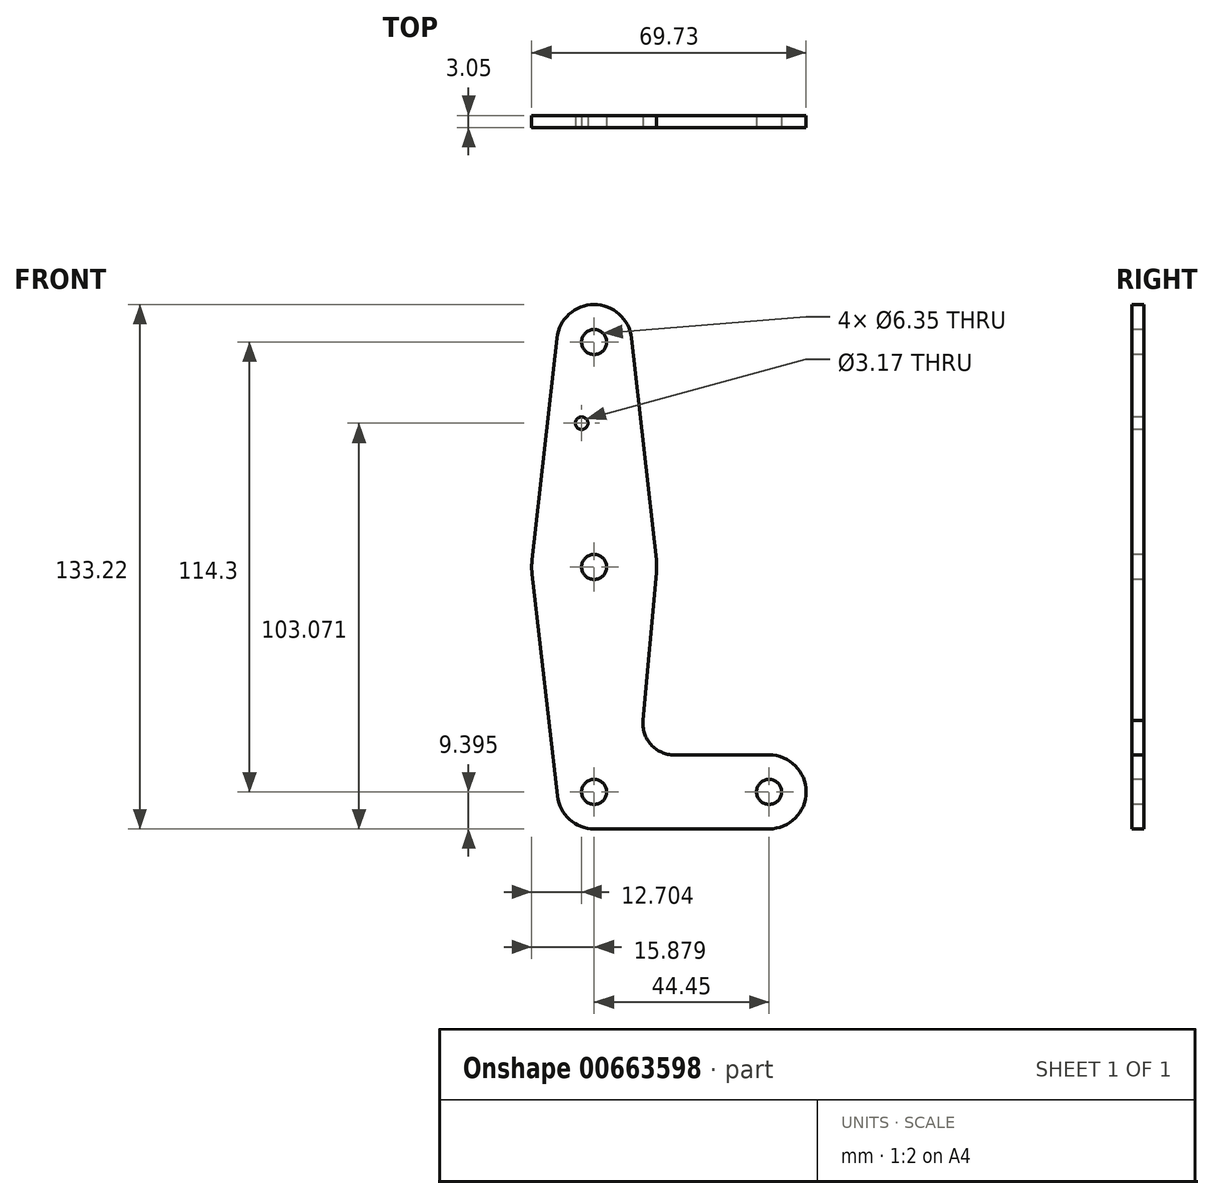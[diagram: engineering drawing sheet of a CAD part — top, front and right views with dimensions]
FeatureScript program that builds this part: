
annotation { "Feature Type Name" : "Feature", "Feature Type Description" : "" }
export const myFeature = defineFeature(function(context is Context, id is Id, definition is map)
    precondition{}
    {
        {
            var Q0;
            Q0=qCreatedBy(makeId("Front.planeOp"),FACE);
            var sketch = newSketch(context, id + "F0", { "sketchPlane" : qUnion([Q0])});
            skLineSegment(sketch, "E0", {"start": v(-45.88, 55.92) * mm, "end": v(-45.88, -58.38) * mm, "construction": true});
            skLineSegment(sketch, "E1", {"start": v(-45.88, -58.38) * mm, "end": v(-1.43, -58.38) * mm, "construction": true});
            skCircle(sketch, "E2", {"center": v(-45.88, 55.92) * mm, "radius": 9.53 * mm});
            skCircle(sketch, "E3", {"center": v(-45.88, -1.23) * mm, "radius": 15.88 * mm});
            skCircle(sketch, "E4", {"center": v(-45.88, -58.38) * mm, "radius": 9.4 * mm});
            skCircle(sketch, "E5", {"center": v(-1.43, -58.38) * mm, "radius": 9.4 * mm});
            skLineSegment(sketch, "E6", {"start": v(-55.35, 56.97) * mm, "end": v(-61.66, 0.53) * mm});
            skLineSegment(sketch, "E7", {"start": v(-61.66, -3) * mm, "end": v(-55.22, -59.45) * mm});
            skLineSegment(sketch, "E8", {"start": v(-45.88, -67.78) * mm, "end": v(-1.43, -67.78) * mm});
            skLineSegment(sketch, "E9", {"start": v(-36.41, 56.97) * mm, "end": v(-30.1, 0.53) * mm});
            skLineSegment(sketch, "E10", {"start": v(-1.43, -48.99) * mm, "end": v(-25.55, -48.99) * mm});
            skPoint(sketch, "E11.orphan", {"position": v(-30.1, -3) * mm});
            skCircle(sketch, "E12", {"center": v(-45.88, -1.23) * mm, "radius": 3.18 * mm});
            skCircle(sketch, "E13", {"center": v(-45.88, -58.38) * mm, "radius": 3.18 * mm});
            skCircle(sketch, "E14", {"center": v(-45.88, 55.92) * mm, "radius": 3.18 * mm});
            skCircle(sketch, "E15", {"center": v(-1.43, -58.38) * mm, "radius": 3.18 * mm});
            skCircle(sketch, "E16", {"center": v(-49.06, 35.3) * mm, "radius": 1.59 * mm});
            skArc(sketch, "E17.filletArc", {"start": v(-33.46, -40.21) * mm, "mid": v(-31.46, -46.36) * mm, "end": v(-25.55, -48.99) * mm});
            skLineSegment(sketch, "E18", {"start": v(-33.46, -40.21) * mm, "end": v(-30.07, -2.66) * mm});
            skText(sketch, "E19", { "text": "ben cahill\n\n0.728in3", "fontName": "OpenSans-Regular.ttf"});
            const initialGuessF0  = {"E19": [0.02328, 0.10574, 1, 0, 0.01949]};
            skSetInitialGuess(sketch, initialGuessF0);
            skSolve(sketch);
        }
        {
            var Q0;
            Q0 = qSketchRegion(id + "F0", true);
            extrude(context, id + "F1", {"entities" : qUnion([Q0]), "oppositeDirection" : true, "depth" : 3.05 * mm, "offsetDistance" : 25.4 * mm});
        }
        {
            var Q0;
            Q0=makeQuery(id+"F1.opExtrude","SWEPT_BODY",BODY,{"disambiguationData":[OSD([sQuery(id+"F0.wireOp",EDGE,"E19.sketch_text.stroke-0"),sQuery(id+"F0.wireOp",EDGE,"E19.sketch_text.stroke-1"),sQuery(id+"F0.wireOp",EDGE,"E19.sketch_text.stroke-2"),sQuery(id+"F0.wireOp",EDGE,"E19.sketch_text.stroke-3"),sQuery(id+"F0.wireOp",EDGE,"E19.sketch_text.stroke-4"),sQuery(id+"F0.wireOp",EDGE,"E19.sketch_text.stroke-5"),sQuery(id+"F0.wireOp",EDGE,"E19.sketch_text.stroke-6"),sQuery(id+"F0.wireOp",EDGE,"E19.sketch_text.stroke-7"),sQuery(id+"F0.wireOp",EDGE,"E19.sketch_text.stroke-8"),sQuery(id+"F0.wireOp",EDGE,"E19.sketch_text.stroke-9"),sQuery(id+"F0.wireOp",EDGE,"E19.sketch_text.stroke-10"),sQuery(id+"F0.wireOp",EDGE,"E19.sketch_text.stroke-11"),sQuery(id+"F0.wireOp",EDGE,"E19.sketch_text.stroke-12"),sQuery(id+"F0.wireOp",EDGE,"E19.sketch_text.stroke-13"),sQuery(id+"F0.wireOp",EDGE,"E19.sketch_text.stroke-14"),sQuery(id+"F0.wireOp",EDGE,"E19.sketch_text.stroke-15"),sQuery(id+"F0.wireOp",EDGE,"E19.sketch_text.stroke-16"),sQuery(id+"F0.wireOp",EDGE,"E19.sketch_text.stroke-17"),sQuery(id+"F0.wireOp",EDGE,"E19.sketch_text.stroke-18"),sQuery(id+"F0.wireOp",EDGE,"E19.sketch_text.stroke-19"),sQuery(id+"F0.wireOp",EDGE,"E19.sketch_text.stroke-20"),sQuery(id+"F0.wireOp",EDGE,"E19.sketch_text.stroke-21"),sQuery(id+"F0.wireOp",EDGE,"E19.sketch_text.stroke-22")])]});
            var Q1;
            Q1=makeQuery(id+"F1.opExtrude","SWEPT_BODY",BODY,{"disambiguationData":[OSD([sQuery(id+"F0.wireOp",EDGE,"E19.sketch_text.stroke-23"),sQuery(id+"F0.wireOp",EDGE,"E19.sketch_text.stroke-24"),sQuery(id+"F0.wireOp",EDGE,"E19.sketch_text.stroke-25"),sQuery(id+"F0.wireOp",EDGE,"E19.sketch_text.stroke-26"),sQuery(id+"F0.wireOp",EDGE,"E19.sketch_text.stroke-27"),sQuery(id+"F0.wireOp",EDGE,"E19.sketch_text.stroke-28"),sQuery(id+"F0.wireOp",EDGE,"E19.sketch_text.stroke-29"),sQuery(id+"F0.wireOp",EDGE,"E19.sketch_text.stroke-30"),sQuery(id+"F0.wireOp",EDGE,"E19.sketch_text.stroke-31"),sQuery(id+"F0.wireOp",EDGE,"E19.sketch_text.stroke-32"),sQuery(id+"F0.wireOp",EDGE,"E19.sketch_text.stroke-33"),sQuery(id+"F0.wireOp",EDGE,"E19.sketch_text.stroke-34"),sQuery(id+"F0.wireOp",EDGE,"E19.sketch_text.stroke-35"),sQuery(id+"F0.wireOp",EDGE,"E19.sketch_text.stroke-36"),sQuery(id+"F0.wireOp",EDGE,"E19.sketch_text.stroke-37"),sQuery(id+"F0.wireOp",EDGE,"E19.sketch_text.stroke-38"),sQuery(id+"F0.wireOp",EDGE,"E19.sketch_text.stroke-39"),sQuery(id+"F0.wireOp",EDGE,"E19.sketch_text.stroke-40"),sQuery(id+"F0.wireOp",EDGE,"E19.sketch_text.stroke-41")])]});
            deleteBodies(context, id + "F2", {"entities" : qUnion([Q0, Q1])});
        }
        {
            var Q0;
            Q0=makeQuery(id+"F1.opExtrude","SWEPT_BODY",BODY,{"disambiguationData":[OSD([sQuery(id+"F0.wireOp",EDGE,"E19.sketch_text.stroke-42"),sQuery(id+"F0.wireOp",EDGE,"E19.sketch_text.stroke-43"),sQuery(id+"F0.wireOp",EDGE,"E19.sketch_text.stroke-44"),sQuery(id+"F0.wireOp",EDGE,"E19.sketch_text.stroke-45"),sQuery(id+"F0.wireOp",EDGE,"E19.sketch_text.stroke-46"),sQuery(id+"F0.wireOp",EDGE,"E19.sketch_text.stroke-47"),sQuery(id+"F0.wireOp",EDGE,"E19.sketch_text.stroke-48"),sQuery(id+"F0.wireOp",EDGE,"E19.sketch_text.stroke-49"),sQuery(id+"F0.wireOp",EDGE,"E19.sketch_text.stroke-50"),sQuery(id+"F0.wireOp",EDGE,"E19.sketch_text.stroke-51"),sQuery(id+"F0.wireOp",EDGE,"E19.sketch_text.stroke-52"),sQuery(id+"F0.wireOp",EDGE,"E19.sketch_text.stroke-53"),sQuery(id+"F0.wireOp",EDGE,"E19.sketch_text.stroke-54"),sQuery(id+"F0.wireOp",EDGE,"E19.sketch_text.stroke-55"),sQuery(id+"F0.wireOp",EDGE,"E19.sketch_text.stroke-56"),sQuery(id+"F0.wireOp",EDGE,"E19.sketch_text.stroke-57"),sQuery(id+"F0.wireOp",EDGE,"E19.sketch_text.stroke-58")])]});
            deleteBodies(context, id + "F3", {"entities" : qUnion([Q0])});
        }
        {
            var Q0;
            Q0=makeQuery(id+"F1.opExtrude","SWEPT_BODY",BODY,{"disambiguationData":[OSD([sQuery(id+"F0.wireOp",EDGE,"E19.sketch_text.stroke-101"),sQuery(id+"F0.wireOp",EDGE,"E19.sketch_text.stroke-102"),sQuery(id+"F0.wireOp",EDGE,"E19.sketch_text.stroke-103"),sQuery(id+"F0.wireOp",EDGE,"E19.sketch_text.stroke-104"),sQuery(id+"F0.wireOp",EDGE,"E19.sketch_text.stroke-105"),sQuery(id+"F0.wireOp",EDGE,"E19.sketch_text.stroke-106"),sQuery(id+"F0.wireOp",EDGE,"E19.sketch_text.stroke-107"),sQuery(id+"F0.wireOp",EDGE,"E19.sketch_text.stroke-108"),sQuery(id+"F0.wireOp",EDGE,"E19.sketch_text.stroke-109"),sQuery(id+"F0.wireOp",EDGE,"E19.sketch_text.stroke-110"),sQuery(id+"F0.wireOp",EDGE,"E19.sketch_text.stroke-111"),sQuery(id+"F0.wireOp",EDGE,"E19.sketch_text.stroke-112"),sQuery(id+"F0.wireOp",EDGE,"E19.sketch_text.stroke-113"),sQuery(id+"F0.wireOp",EDGE,"E19.sketch_text.stroke-114"),sQuery(id+"F0.wireOp",EDGE,"E19.sketch_text.stroke-115"),sQuery(id+"F0.wireOp",EDGE,"E19.sketch_text.stroke-116"),sQuery(id+"F0.wireOp",EDGE,"E19.sketch_text.stroke-117"),sQuery(id+"F0.wireOp",EDGE,"E19.sketch_text.stroke-118")])]});
            deleteBodies(context, id + "F4", {"entities" : qUnion([Q0])});
        }
        {
            var Q0;
            Q0=makeQuery(id+"F1.opExtrude","SWEPT_BODY",BODY,{"disambiguationData":[OSD([sQuery(id+"F0.wireOp",EDGE,"E19.sketch_text.stroke-74"),sQuery(id+"F0.wireOp",EDGE,"E19.sketch_text.stroke-75"),sQuery(id+"F0.wireOp",EDGE,"E19.sketch_text.stroke-76"),sQuery(id+"F0.wireOp",EDGE,"E19.sketch_text.stroke-77"),sQuery(id+"F0.wireOp",EDGE,"E19.sketch_text.stroke-78"),sQuery(id+"F0.wireOp",EDGE,"E19.sketch_text.stroke-79"),sQuery(id+"F0.wireOp",EDGE,"E19.sketch_text.stroke-80"),sQuery(id+"F0.wireOp",EDGE,"E19.sketch_text.stroke-81"),sQuery(id+"F0.wireOp",EDGE,"E19.sketch_text.stroke-82"),sQuery(id+"F0.wireOp",EDGE,"E19.sketch_text.stroke-83"),sQuery(id+"F0.wireOp",EDGE,"E19.sketch_text.stroke-84"),sQuery(id+"F0.wireOp",EDGE,"E19.sketch_text.stroke-85"),sQuery(id+"F0.wireOp",EDGE,"E19.sketch_text.stroke-86"),sQuery(id+"F0.wireOp",EDGE,"E19.sketch_text.stroke-87"),sQuery(id+"F0.wireOp",EDGE,"E19.sketch_text.stroke-88"),sQuery(id+"F0.wireOp",EDGE,"E19.sketch_text.stroke-89"),sQuery(id+"F0.wireOp",EDGE,"E19.sketch_text.stroke-90"),sQuery(id+"F0.wireOp",EDGE,"E19.sketch_text.stroke-91"),sQuery(id+"F0.wireOp",EDGE,"E19.sketch_text.stroke-92"),sQuery(id+"F0.wireOp",EDGE,"E19.sketch_text.stroke-93"),sQuery(id+"F0.wireOp",EDGE,"E19.sketch_text.stroke-94"),sQuery(id+"F0.wireOp",EDGE,"E19.sketch_text.stroke-95"),sQuery(id+"F0.wireOp",EDGE,"E19.sketch_text.stroke-96"),sQuery(id+"F0.wireOp",EDGE,"E19.sketch_text.stroke-97"),sQuery(id+"F0.wireOp",EDGE,"E19.sketch_text.stroke-98"),sQuery(id+"F0.wireOp",EDGE,"E19.sketch_text.stroke-99"),sQuery(id+"F0.wireOp",EDGE,"E19.sketch_text.stroke-100")])]});
            deleteBodies(context, id + "F5", {"entities" : qUnion([Q0])});
        }
        {
            var Q0;
            Q0=makeQuery(id+"F1.opExtrude","SWEPT_BODY",BODY,{"disambiguationData":[OSD([sQuery(id+"F0.wireOp",EDGE,"E19.sketch_text.stroke-59"),sQuery(id+"F0.wireOp",EDGE,"E19.sketch_text.stroke-60"),sQuery(id+"F0.wireOp",EDGE,"E19.sketch_text.stroke-61"),sQuery(id+"F0.wireOp",EDGE,"E19.sketch_text.stroke-62"),sQuery(id+"F0.wireOp",EDGE,"E19.sketch_text.stroke-63"),sQuery(id+"F0.wireOp",EDGE,"E19.sketch_text.stroke-64"),sQuery(id+"F0.wireOp",EDGE,"E19.sketch_text.stroke-65"),sQuery(id+"F0.wireOp",EDGE,"E19.sketch_text.stroke-66"),sQuery(id+"F0.wireOp",EDGE,"E19.sketch_text.stroke-67"),sQuery(id+"F0.wireOp",EDGE,"E19.sketch_text.stroke-68"),sQuery(id+"F0.wireOp",EDGE,"E19.sketch_text.stroke-69"),sQuery(id+"F0.wireOp",EDGE,"E19.sketch_text.stroke-70"),sQuery(id+"F0.wireOp",EDGE,"E19.sketch_text.stroke-71"),sQuery(id+"F0.wireOp",EDGE,"E19.sketch_text.stroke-72"),sQuery(id+"F0.wireOp",EDGE,"E19.sketch_text.stroke-73")])]});
            var Q1;
            Q1=makeQuery(id+"F1.opExtrude","SWEPT_BODY",BODY,{"disambiguationData":[OSD([sQuery(id+"F0.wireOp",EDGE,"E19.sketch_text.stroke-119"),sQuery(id+"F0.wireOp",EDGE,"E19.sketch_text.stroke-120"),sQuery(id+"F0.wireOp",EDGE,"E19.sketch_text.stroke-121"),sQuery(id+"F0.wireOp",EDGE,"E19.sketch_text.stroke-122")])]});
            var Q2;
            Q2=makeQuery(id+"F1.opExtrude","SWEPT_BODY",BODY,{"disambiguationData":[OSD([sQuery(id+"F0.wireOp",EDGE,"E19.sketch_text.stroke-123"),sQuery(id+"F0.wireOp",EDGE,"E19.sketch_text.stroke-124"),sQuery(id+"F0.wireOp",EDGE,"E19.sketch_text.stroke-125"),sQuery(id+"F0.wireOp",EDGE,"E19.sketch_text.stroke-126"),sQuery(id+"F0.wireOp",EDGE,"E19.sketch_text.stroke-127"),sQuery(id+"F0.wireOp",EDGE,"E19.sketch_text.stroke-128"),sQuery(id+"F0.wireOp",EDGE,"E19.sketch_text.stroke-129"),sQuery(id+"F0.wireOp",EDGE,"E19.sketch_text.stroke-130")])]});
            deleteBodies(context, id + "F6", {"entities" : qUnion([Q0, Q1, Q2])});
        }
        {
            var Q0;
            Q0=makeQuery(id+"F1.opExtrude","SWEPT_BODY",BODY,{"disambiguationData":[OSD([sQuery(id+"F0.wireOp",EDGE,"E19.sketch_text.stroke-131"),sQuery(id+"F0.wireOp",EDGE,"E19.sketch_text.stroke-132"),sQuery(id+"F0.wireOp",EDGE,"E19.sketch_text.stroke-133"),sQuery(id+"F0.wireOp",EDGE,"E19.sketch_text.stroke-134")])]});
            var Q1;
            Q1=makeQuery(id+"F1.opExtrude","SWEPT_BODY",BODY,{"disambiguationData":[OSD([sQuery(id+"F0.wireOp",EDGE,"E19.sketch_text.stroke-135"),sQuery(id+"F0.wireOp",EDGE,"E19.sketch_text.stroke-136"),sQuery(id+"F0.wireOp",EDGE,"E19.sketch_text.stroke-137"),sQuery(id+"F0.wireOp",EDGE,"E19.sketch_text.stroke-138")])]});
            var Q2;
            Q2=makeQuery(id+"F1.opExtrude","SWEPT_BODY",BODY,{"disambiguationData":[OSD([sQuery(id+"F0.wireOp",EDGE,"E19.sketch_text.stroke-139"),sQuery(id+"F0.wireOp",EDGE,"E19.sketch_text.stroke-140"),sQuery(id+"F0.wireOp",EDGE,"E19.sketch_text.stroke-141"),sQuery(id+"F0.wireOp",EDGE,"E19.sketch_text.stroke-142"),sQuery(id+"F0.wireOp",EDGE,"E19.sketch_text.stroke-143"),sQuery(id+"F0.wireOp",EDGE,"E19.sketch_text.stroke-144"),sQuery(id+"F0.wireOp",EDGE,"E19.sketch_text.stroke-145"),sQuery(id+"F0.wireOp",EDGE,"E19.sketch_text.stroke-146"),sQuery(id+"F0.wireOp",EDGE,"E19.sketch_text.stroke-147"),sQuery(id+"F0.wireOp",EDGE,"E19.sketch_text.stroke-148"),sQuery(id+"F0.wireOp",EDGE,"E19.sketch_text.stroke-149"),sQuery(id+"F0.wireOp",EDGE,"E19.sketch_text.stroke-150"),sQuery(id+"F0.wireOp",EDGE,"E19.sketch_text.stroke-151"),sQuery(id+"F0.wireOp",EDGE,"E19.sketch_text.stroke-152"),sQuery(id+"F0.wireOp",EDGE,"E19.sketch_text.stroke-153"),sQuery(id+"F0.wireOp",EDGE,"E19.sketch_text.stroke-154")])]});
            deleteBodies(context, id + "F7", {"entities" : qUnion([Q0, Q1, Q2])});
        }
        {
            var Q0;
            Q0=makeQuery(id+"F1.opExtrude","SWEPT_BODY",BODY,{"disambiguationData":[OSD([sQuery(id+"F0.wireOp",EDGE,"E19.sketch_text.stroke-155"),sQuery(id+"F0.wireOp",EDGE,"E19.sketch_text.stroke-156"),sQuery(id+"F0.wireOp",EDGE,"E19.sketch_text.stroke-157"),sQuery(id+"F0.wireOp",EDGE,"E19.sketch_text.stroke-158"),sQuery(id+"F0.wireOp",EDGE,"E19.sketch_text.stroke-159"),sQuery(id+"F0.wireOp",EDGE,"E19.sketch_text.stroke-160"),sQuery(id+"F0.wireOp",EDGE,"E19.sketch_text.stroke-161"),sQuery(id+"F0.wireOp",EDGE,"E19.sketch_text.stroke-162")])]});
            deleteBodies(context, id + "F8", {"entities" : qUnion([Q0])});
        }
        {
            var Q0;
            Q0=makeQuery(id+"F1.opExtrude","SWEPT_BODY",BODY,{"disambiguationData":[OSD([sQuery(id+"F0.wireOp",EDGE,"E19.sketch_text.stroke-163"),sQuery(id+"F0.wireOp",EDGE,"E19.sketch_text.stroke-164"),sQuery(id+"F0.wireOp",EDGE,"E19.sketch_text.stroke-165"),sQuery(id+"F0.wireOp",EDGE,"E19.sketch_text.stroke-166"),sQuery(id+"F0.wireOp",EDGE,"E19.sketch_text.stroke-167"),sQuery(id+"F0.wireOp",EDGE,"E19.sketch_text.stroke-168"),sQuery(id+"F0.wireOp",EDGE,"E19.sketch_text.stroke-169")])]});
            deleteBodies(context, id + "F9", {"entities" : qUnion([Q0])});
        }
        {
            var Q0;
            Q0=makeQuery(id+"F1.opExtrude","SWEPT_BODY",BODY,{"disambiguationData":[OSD([sQuery(id+"F0.wireOp",EDGE,"E19.sketch_text.stroke-170"),sQuery(id+"F0.wireOp",EDGE,"E19.sketch_text.stroke-171"),sQuery(id+"F0.wireOp",EDGE,"E19.sketch_text.stroke-172"),sQuery(id+"F0.wireOp",EDGE,"E19.sketch_text.stroke-173"),sQuery(id+"F0.wireOp",EDGE,"E19.sketch_text.stroke-174"),sQuery(id+"F0.wireOp",EDGE,"E19.sketch_text.stroke-175"),sQuery(id+"F0.wireOp",EDGE,"E19.sketch_text.stroke-176"),sQuery(id+"F0.wireOp",EDGE,"E19.sketch_text.stroke-177"),sQuery(id+"F0.wireOp",EDGE,"E19.sketch_text.stroke-178"),sQuery(id+"F0.wireOp",EDGE,"E19.sketch_text.stroke-179"),sQuery(id+"F0.wireOp",EDGE,"E19.sketch_text.stroke-180"),sQuery(id+"F0.wireOp",EDGE,"E19.sketch_text.stroke-181"),sQuery(id+"F0.wireOp",EDGE,"E19.sketch_text.stroke-182"),sQuery(id+"F0.wireOp",EDGE,"E19.sketch_text.stroke-183"),sQuery(id+"F0.wireOp",EDGE,"E19.sketch_text.stroke-184"),sQuery(id+"F0.wireOp",EDGE,"E19.sketch_text.stroke-185"),sQuery(id+"F0.wireOp",EDGE,"E19.sketch_text.stroke-186"),sQuery(id+"F0.wireOp",EDGE,"E19.sketch_text.stroke-187"),sQuery(id+"F0.wireOp",EDGE,"E19.sketch_text.stroke-188"),sQuery(id+"F0.wireOp",EDGE,"E19.sketch_text.stroke-189")])]});
            deleteBodies(context, id + "F10", {"entities" : qUnion([Q0])});
        }
        {
            var Q0;
            Q0=makeQuery(id+"F1.opExtrude","SWEPT_BODY",BODY,{"disambiguationData":[OSD([sQuery(id+"F0.wireOp",EDGE,"E19.sketch_text.stroke-190"),sQuery(id+"F0.wireOp",EDGE,"E19.sketch_text.stroke-191"),sQuery(id+"F0.wireOp",EDGE,"E19.sketch_text.stroke-192"),sQuery(id+"F0.wireOp",EDGE,"E19.sketch_text.stroke-193"),sQuery(id+"F0.wireOp",EDGE,"E19.sketch_text.stroke-194"),sQuery(id+"F0.wireOp",EDGE,"E19.sketch_text.stroke-195"),sQuery(id+"F0.wireOp",EDGE,"E19.sketch_text.stroke-196"),sQuery(id+"F0.wireOp",EDGE,"E19.sketch_text.stroke-197"),sQuery(id+"F0.wireOp",EDGE,"E19.sketch_text.stroke-198"),sQuery(id+"F0.wireOp",EDGE,"E19.sketch_text.stroke-199"),sQuery(id+"F0.wireOp",EDGE,"E19.sketch_text.stroke-200"),sQuery(id+"F0.wireOp",EDGE,"E19.sketch_text.stroke-201"),sQuery(id+"F0.wireOp",EDGE,"E19.sketch_text.stroke-202"),sQuery(id+"F0.wireOp",EDGE,"E19.sketch_text.stroke-203"),sQuery(id+"F0.wireOp",EDGE,"E19.sketch_text.stroke-204"),sQuery(id+"F0.wireOp",EDGE,"E19.sketch_text.stroke-205"),sQuery(id+"F0.wireOp",EDGE,"E19.sketch_text.stroke-206"),sQuery(id+"F0.wireOp",EDGE,"E19.sketch_text.stroke-207"),sQuery(id+"F0.wireOp",EDGE,"E19.sketch_text.stroke-208"),sQuery(id+"F0.wireOp",EDGE,"E19.sketch_text.stroke-209"),sQuery(id+"F0.wireOp",EDGE,"E19.sketch_text.stroke-210"),sQuery(id+"F0.wireOp",EDGE,"E19.sketch_text.stroke-211"),sQuery(id+"F0.wireOp",EDGE,"E19.sketch_text.stroke-212"),sQuery(id+"F0.wireOp",EDGE,"E19.sketch_text.stroke-213"),sQuery(id+"F0.wireOp",EDGE,"E19.sketch_text.stroke-214"),sQuery(id+"F0.wireOp",EDGE,"E19.sketch_text.stroke-215"),sQuery(id+"F0.wireOp",EDGE,"E19.sketch_text.stroke-216"),sQuery(id+"F0.wireOp",EDGE,"E19.sketch_text.stroke-217"),sQuery(id+"F0.wireOp",EDGE,"E19.sketch_text.stroke-218"),sQuery(id+"F0.wireOp",EDGE,"E19.sketch_text.stroke-219"),sQuery(id+"F0.wireOp",EDGE,"E19.sketch_text.stroke-220")])]});
            deleteBodies(context, id + "F11", {"entities" : qUnion([Q0])});
        }
        {
            var Q0;
            Q0=makeQuery(id+"F1.opExtrude","SWEPT_BODY",BODY,{"disambiguationData":[OSD([sQuery(id+"F0.wireOp",EDGE,"E19.sketch_text.stroke-221"),sQuery(id+"F0.wireOp",EDGE,"E19.sketch_text.stroke-222"),sQuery(id+"F0.wireOp",EDGE,"E19.sketch_text.stroke-223"),sQuery(id+"F0.wireOp",EDGE,"E19.sketch_text.stroke-224")])]});
            deleteBodies(context, id + "F12", {"entities" : qUnion([Q0])});
        }
        {
            var Q0;
            Q0=makeQuery(id+"F1.opExtrude","SWEPT_BODY",BODY,{"disambiguationData":[OSD([sQuery(id+"F0.wireOp",EDGE,"E19.sketch_text.stroke-225"),sQuery(id+"F0.wireOp",EDGE,"E19.sketch_text.stroke-226"),sQuery(id+"F0.wireOp",EDGE,"E19.sketch_text.stroke-227"),sQuery(id+"F0.wireOp",EDGE,"E19.sketch_text.stroke-228"),sQuery(id+"F0.wireOp",EDGE,"E19.sketch_text.stroke-229"),sQuery(id+"F0.wireOp",EDGE,"E19.sketch_text.stroke-230"),sQuery(id+"F0.wireOp",EDGE,"E19.sketch_text.stroke-231"),sQuery(id+"F0.wireOp",EDGE,"E19.sketch_text.stroke-232")])]});
            var Q1;
            Q1=makeQuery(id+"F1.opExtrude","SWEPT_BODY",BODY,{"disambiguationData":[OSD([sQuery(id+"F0.wireOp",EDGE,"E19.sketch_text.stroke-233"),sQuery(id+"F0.wireOp",EDGE,"E19.sketch_text.stroke-234"),sQuery(id+"F0.wireOp",EDGE,"E19.sketch_text.stroke-235"),sQuery(id+"F0.wireOp",EDGE,"E19.sketch_text.stroke-236"),sQuery(id+"F0.wireOp",EDGE,"E19.sketch_text.stroke-237"),sQuery(id+"F0.wireOp",EDGE,"E19.sketch_text.stroke-238"),sQuery(id+"F0.wireOp",EDGE,"E19.sketch_text.stroke-239"),sQuery(id+"F0.wireOp",EDGE,"E19.sketch_text.stroke-240"),sQuery(id+"F0.wireOp",EDGE,"E19.sketch_text.stroke-241"),sQuery(id+"F0.wireOp",EDGE,"E19.sketch_text.stroke-242"),sQuery(id+"F0.wireOp",EDGE,"E19.sketch_text.stroke-243"),sQuery(id+"F0.wireOp",EDGE,"E19.sketch_text.stroke-244"),sQuery(id+"F0.wireOp",EDGE,"E19.sketch_text.stroke-245"),sQuery(id+"F0.wireOp",EDGE,"E19.sketch_text.stroke-246"),sQuery(id+"F0.wireOp",EDGE,"E19.sketch_text.stroke-247"),sQuery(id+"F0.wireOp",EDGE,"E19.sketch_text.stroke-248"),sQuery(id+"F0.wireOp",EDGE,"E19.sketch_text.stroke-249")])]});
            deleteBodies(context, id + "F13", {"entities" : qUnion([Q0, Q1])});
        }
        {
            var Q0;
            Q0=makeQuery(id+"F1.opExtrude","SWEPT_BODY",BODY,{"disambiguationData":[OSD([sQuery(id+"F0.wireOp",EDGE,"E19.sketch_text.stroke-250"),sQuery(id+"F0.wireOp",EDGE,"E19.sketch_text.stroke-251"),sQuery(id+"F0.wireOp",EDGE,"E19.sketch_text.stroke-252"),sQuery(id+"F0.wireOp",EDGE,"E19.sketch_text.stroke-253"),sQuery(id+"F0.wireOp",EDGE,"E19.sketch_text.stroke-254"),sQuery(id+"F0.wireOp",EDGE,"E19.sketch_text.stroke-255"),sQuery(id+"F0.wireOp",EDGE,"E19.sketch_text.stroke-256"),sQuery(id+"F0.wireOp",EDGE,"E19.sketch_text.stroke-257"),sQuery(id+"F0.wireOp",EDGE,"E19.sketch_text.stroke-258"),sQuery(id+"F0.wireOp",EDGE,"E19.sketch_text.stroke-259"),sQuery(id+"F0.wireOp",EDGE,"E19.sketch_text.stroke-260"),sQuery(id+"F0.wireOp",EDGE,"E19.sketch_text.stroke-261"),sQuery(id+"F0.wireOp",EDGE,"E19.sketch_text.stroke-262"),sQuery(id+"F0.wireOp",EDGE,"E19.sketch_text.stroke-263"),sQuery(id+"F0.wireOp",EDGE,"E19.sketch_text.stroke-264"),sQuery(id+"F0.wireOp",EDGE,"E19.sketch_text.stroke-265"),sQuery(id+"F0.wireOp",EDGE,"E19.sketch_text.stroke-266"),sQuery(id+"F0.wireOp",EDGE,"E19.sketch_text.stroke-267"),sQuery(id+"F0.wireOp",EDGE,"E19.sketch_text.stroke-268"),sQuery(id+"F0.wireOp",EDGE,"E19.sketch_text.stroke-269"),sQuery(id+"F0.wireOp",EDGE,"E19.sketch_text.stroke-270"),sQuery(id+"F0.wireOp",EDGE,"E19.sketch_text.stroke-271"),sQuery(id+"F0.wireOp",EDGE,"E19.sketch_text.stroke-272"),sQuery(id+"F0.wireOp",EDGE,"E19.sketch_text.stroke-273"),sQuery(id+"F0.wireOp",EDGE,"E19.sketch_text.stroke-274"),sQuery(id+"F0.wireOp",EDGE,"E19.sketch_text.stroke-275"),sQuery(id+"F0.wireOp",EDGE,"E19.sketch_text.stroke-276"),sQuery(id+"F0.wireOp",EDGE,"E19.sketch_text.stroke-277")])]});
            deleteBodies(context, id + "F14", {"entities" : qUnion([Q0])});
        }
    });
